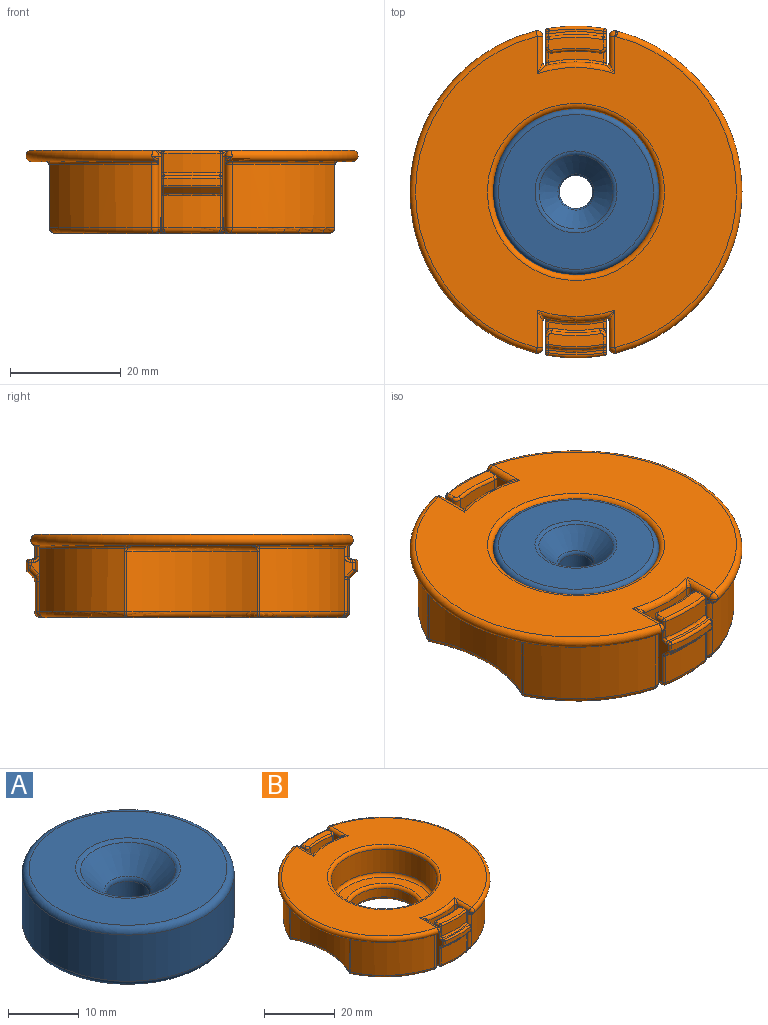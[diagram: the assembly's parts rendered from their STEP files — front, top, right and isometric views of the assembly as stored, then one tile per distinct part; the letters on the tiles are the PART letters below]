
ASSEMBLY  parts=2 mates=1
PART A: 10 faces, bbox 32.5x32.5x10 mm
  f0: cylinder r=3mm len=6mm, axis (0,0,-1), area 86.4mm2, adj f6,f7
  f1: cylinder r=15mm len=30mm, axis (0,0,-1), area 754mm2, adj f8,f9
  f2: plane 28x28mm, normal (0,0,1), area 443.1mm2, adj f5,f9
  f3: plane 28x28mm, normal (0,0,-1), area 565.5mm2, adj f7,f8
  f4: cone r=3mm half-angle=45deg, axis (0,0,1), area 151.7mm2, adj f5,f6
  f5: torus R=7.41mm, axis (0,0,1), area 34.7mm2, adj f2,f4
  f6: torus R=4mm, axis (0,0,-1), area 15.3mm2, adj f0,f4
  f7: torus R=4mm, axis (0,0,1), area 33.2mm2, adj f0,f3
  f8: torus R=14mm, axis (0,0,1), area 144.5mm2, adj f1,f3
  f9: torus R=14mm, axis (0,0,1), area 144.5mm2, adj f1,f2
PART B: 237 faces, bbox 65.5x81.4x21.4 mm
  f0: plane 25.09x5.42mm, normal (0,0,-1), area 77.3mm2, adj f1,f234,f235,f236
  f1: bspline ~2.39x0.69mm, area 0.5mm2, adj f0,f2,f233
  f2: torus R=29mm, axis (0,0,1), area 19.7mm2, adj f1,f3,f232,f236
  f3: torus R=1.5mm, axis (0,0,1), area 1.1mm2, adj f2,f4,f230,f231
  f4: bspline ~1.67x1mm, area 0.4mm2, adj f3,f5,f229
  f5: cylinder r=0.5mm len=0.5mm, axis (0,1,0), area 0.1mm2, adj f4,f6,f229,f230
  f6: torus R=0.5mm, axis (0,0,1), area 0.2mm2, adj f5,f7,f228,f230
  f7: cylinder r=1mm len=1.24mm, axis (0,0,1), area 0.5mm2, adj f6,f8,f228,f229
  f8: sphere r=1mm, area 2.3mm2, adj f7,f9,f236
  f9: cylinder r=1mm len=6.76mm, axis (0,-1,0), area 9.1mm2, adj f8,f10,f227,f229
  f10: plane 58x56.29mm, normal (0,0,1), area 1653.5mm2, adj f9,f11,f221,f222,f223,f224,f225,f226
  f11: torus R=22.5mm, axis (0,0,1), area 19.9mm2, adj f10,f12,f220,f227
  f12: bspline ~1.98x1.62mm, area 0.7mm2, adj f11,f13,f225
  f13: cylinder r=0.5mm len=13mm, axis (0,0,1), area 11.2mm2, adj f12,f14,f217,f218,f219,f220
  f14: bspline ~1.2x1.19mm, area 0.6mm2, adj f13,f15,f216,f217,f220
  f15: torus R=24mm, axis (0,0,1), area 7.8mm2, adj f14,f16,f215,f220
  f16: bspline ~1.22x1.13mm, area 0.6mm2, adj f15,f17,f213,f214,f220
  f17: cylinder r=0.5mm len=1.5mm, axis (0,0,1), area 0.6mm2, adj f16,f18,f212,f214
  f18: bspline ~1.38x1.19mm, area 0.4mm2, adj f17,f19,f210,f211
  f19: bspline ~1.98x1.62mm, area 0.7mm2, adj f18,f20,f210,f214
  f20: cylinder r=1mm len=5.21mm, axis (0,1,0), area 6.6mm2, adj f19,f21,f156,f229
  f21: sphere r=1mm, area 1.2mm2, adj f20,f22,f231
  f22: torus R=27.5mm, axis (0,0,1), area 38.3mm2, adj f21,f23,f156,f232
  f23: bspline ~1.14x1.11mm, area 0.3mm2, adj f22,f24,f155
  f24: torus R=27.68mm, axis (0,0,1), area 38.5mm2, adj f23,f25,f154,f156
  f25: bspline ~1.14x1.11mm, area 0.3mm2, adj f24,f26,f153
  f26: torus R=27.5mm, axis (0,0,1), area 38.3mm2, adj f25,f27,f151,f156
  f27: sphere r=1mm, area 1.8mm2, adj f26,f28,f150
  f28: cylinder r=1mm len=5.21mm, axis (0,1,0), area 6.6mm2, adj f27,f29,f140,f156
  f29: bspline ~1.98x1.62mm, area 0.7mm2, adj f28,f30,f137,f138
  f30: bspline ~1.38x1.19mm, area 0.4mm2, adj f29,f31,f136,f137
  f31: cylinder r=0.5mm len=1.5mm, axis (0,0,1), area 0.6mm2, adj f30,f32,f135,f138
  f32: bspline ~1.2x1.19mm, area 0.6mm2, adj f31,f33,f133,f134,f138
  f33: cylinder r=23.5mm len=10.77mm, axis (0,0,1), area 114.2mm2, adj f32,f34,f131,f133,f138,f222
  f34: bspline ~1.22x1.13mm, area 0.6mm2, adj f33,f35,f130,f131,f133
  f35: cylinder r=0.5mm len=1.5mm, axis (0,0,1), area 0.6mm2, adj f34,f36,f129,f131
  f36: bspline ~1.38x1.19mm, area 0.4mm2, adj f35,f37,f38,f87
  f37: torus R=22.5mm, axis (0,0,1), area 1.3mm2, adj f36,f87,f156
  f38: cylinder r=1mm len=5.5mm, axis (0,1,0), area 7.4mm2, adj f36,f39,f129,f156
  f39: bspline ~1.13x1mm, area 0.5mm2, adj f38,f40,f86
  f40: cylinder r=0.5mm len=5.79mm, axis (0,0,1), area 4mm2, adj f39,f41,f85,f129
  f41: bspline ~0.99x0.68mm, area 0.4mm2, adj f40,f42,f84,f129
  f42: bspline ~16.41x16.19mm, area 1.2mm2, adj f41,f43,f83,f129
  f43: cone r=30mm half-angle=45deg, axis (0,0,1), area 17.4mm2, adj f42,f44,f79,f84
  f44: torus R=29.5mm, axis (0,0,-1), area 4mm2, adj f43,f45,f78,f83
  f45: cylinder r=30mm len=10.17mm, axis (0,0,1), area 13.2mm2, adj f44,f46,f76,f77
  f46: torus R=29.5mm, axis (0,0,1), area 8mm2, adj f45,f47,f74,f75
  f47: plane 10x0.93mm, normal (0,0,1), area 5mm2, adj f46,f48,f72,f73
  f48: torus R=29mm, axis (0,0,1), area 7.9mm2, adj f47,f49,f70,f71
  f49: bspline ~1.25x1.18mm, area 0.8mm2, adj f48,f50,f73,f129
  f50: cylinder r=0.5mm len=3.5mm, axis (0,0,1), area 2.4mm2, adj f49,f51,f71,f129
  f51: sphere r=0.5mm, area 0.3mm2, adj f50,f52,f69
  f52: torus R=28mm, axis (0,0,1), area 8mm2, adj f51,f53,f67,f71
  f53: plane 10x2.39mm, normal (0,0,1), area 20mm2, adj f52,f54,f64,f65,f66,f69
  f54: torus R=0.5mm, axis (0,0,1), area 1.1mm2, adj f53,f55,f64,f69
  f55: cylinder r=1mm len=11mm, axis (0,0,1), area 19.2mm2, adj f54,f56,f63,f129
  f56: torus R=1.5mm, axis (0,0,1), area 1mm2, adj f55,f57,f61,f62
  f57: torus R=25mm, axis (0,0,1), area 6.8mm2, adj f56,f58,f61,f63
  f58: torus R=1.5mm, axis (0,0,1), area 1mm2, adj f57,f59,f60,f61
  f59: cylinder r=1mm len=11mm, axis (0,0,1), area 19.2mm2, adj f58,f63,f65,f135
  f60: bspline ~1.67x1mm, area 0.4mm2, adj f58,f134,f135
  f61: plane 10x1.53mm, normal (0,0,1), area 10.2mm2, adj f56,f57,f58,f130,f133,f134
  f62: bspline ~1.67x1mm, area 0.5mm2, adj f56,f129,f130
  f63: cylinder r=25.5mm len=11mm, axis (0,0,1), area 95.7mm2, adj f55,f57,f59,f64
  f64: torus R=26mm, axis (0,0,1), area 6.9mm2, adj f53,f54,f63,f65
  f65: torus R=0.5mm, axis (0,0,1), area 1.1mm2, adj f53,f59,f64,f66
  f66: cylinder r=0.5mm len=1.44mm, axis (0,1,0), area 1.1mm2, adj f53,f65,f67,f135
  f67: sphere r=0.5mm, area 0.3mm2, adj f52,f66,f68
  f68: cylinder r=0.5mm len=3.5mm, axis (0,0,1), area 2.4mm2, adj f67,f70,f71,f135
  f69: cylinder r=0.5mm len=1.44mm, axis (0,-1,0), area 1.1mm2, adj f51,f53,f54,f129
  f70: bspline ~1.22x1.18mm, area 0.8mm2, adj f48,f68,f72,f135
  f71: cylinder r=28.5mm len=10.18mm, axis (0,0,1), area 35.8mm2, adj f48,f50,f52,f68
  f72: cylinder r=0.5mm len=0.51mm, axis (0,1,0), area 0.4mm2, adj f47,f70,f74,f135
  f73: cylinder r=0.5mm len=0.51mm, axis (0,-1,0), area 0.4mm2, adj f47,f49,f75,f129
  f74: sphere r=0.5mm, area 0.4mm2, adj f46,f72,f76
  f75: sphere r=0.5mm, area 0.2mm2, adj f46,f73,f77
  f76: cylinder r=0.5mm len=1.29mm, axis (0,0,1), area 0.9mm2, adj f45,f74,f78,f135
  f77: cylinder r=0.5mm len=1.29mm, axis (0,0,1), area 0.9mm2, adj f45,f75,f83,f129
  f78: sphere r=0.5mm, area 0.1mm2, adj f44,f76,f79
  f79: bspline ~16.41x16.19mm, area 1.2mm2, adj f43,f78,f80,f135
  f80: bspline ~0.96x0.74mm, area 0.4mm2, adj f79,f81,f84,f135
  f81: cylinder r=0.5mm len=5.79mm, axis (0,0,1), area 4mm2, adj f80,f82,f85,f135
  f82: bspline ~1.13x1mm, area 0.5mm2, adj f81,f86,f136
  f83: sphere r=0.5mm, area 0.1mm2, adj f42,f44,f77
  f84: torus R=29mm, axis (0,0,-1), area 4mm2, adj f41,f43,f80,f85
  f85: cylinder r=28.5mm len=10.18mm, axis (0,0,1), area 59.3mm2, adj f40,f81,f84,f86
  f86: torus R=27.5mm, axis (0,0,1), area 15.2mm2, adj f39,f82,f85,f156
  f87: bspline ~1.98x1.62mm, area 0.7mm2, adj f36,f37,f88,f131
  f88: cylinder r=1mm len=5.21mm, axis (0,-1,0), area 6.6mm2, adj f87,f89,f128,f156
  f89: sphere r=1mm, area 1.8mm2, adj f88,f90,f127
  f90: torus R=27.5mm, axis (0,0,1), area 38.3mm2, adj f89,f91,f126,f156
  f91: bspline ~1.14x1.11mm, area 0.3mm2, adj f90,f92,f125
  f92: cylinder r=0.5mm len=11mm, axis (0,0,-1), area 5mm2, adj f91,f93,f124,f126
  f93: cylinder r=26.68mm len=23.57mm, axis (0,0,1), area 268.6mm2, adj f92,f94,f123,f125
  f94: torus R=25.68mm, axis (0,0,1), area 35.7mm2, adj f93,f95,f122,f124
  f95: plane 25.09x5.42mm, normal (0,0,-1), area 77.3mm2, adj f94,f96,f106,f224
  f96: bspline ~2.18x0.58mm, area 0.5mm2, adj f95,f97,f124
  f97: torus R=29mm, axis (0,0,1), area 19.7mm2, adj f96,f98,f126,f224
  f98: torus R=1.5mm, axis (0,0,1), area 1.1mm2, adj f97,f99,f105,f127
  f99: bspline ~1.67x1mm, area 0.4mm2, adj f98,f100,f128
  f100: cylinder r=0.5mm len=0.5mm, axis (0,1,0), area 0.1mm2, adj f99,f101,f105,f128
  f101: torus R=0.5mm, axis (0,0,1), area 0.2mm2, adj f100,f102,f104,f105
  f102: cylinder r=1mm len=1.24mm, axis (0,0,1), area 0.5mm2, adj f101,f103,f104,f128
  f103: sphere r=1mm, area 1.8mm2, adj f102,f223,f224
  f104: bspline ~1.25x1.06mm, area 0.6mm2, adj f101,f102,f224
  f105: plane 0.88x0.25mm, normal (0,0,-1), area 0.1mm2, adj f98,f100,f101,f224
  f106: bspline ~2.39x0.69mm, area 0.5mm2, adj f95,f107,f122
  f107: torus R=29mm, axis (0,0,1), area 19.7mm2, adj f106,f108,f121,f224
  f108: torus R=1.5mm, axis (0,0,1), area 1.1mm2, adj f107,f109,f115,f120
  f109: bspline ~1.67x1mm, area 0.5mm2, adj f108,f110,f219
  f110: cylinder r=0.5mm len=0.5mm, axis (0,-1,0), area 0.1mm2, adj f109,f111,f120,f219
  f111: torus R=0.5mm, axis (0,0,1), area 0.2mm2, adj f110,f112,f114,f120
  f112: cylinder r=1mm len=1.24mm, axis (0,0,1), area 0.5mm2, adj f111,f113,f114,f219
  f113: sphere r=1mm, area 1.2mm2, adj f112,f224,f225
  f114: bspline ~1.25x1.06mm, area 0.6mm2, adj f111,f112,f224
  f115: cylinder r=1mm len=11.5mm, axis (0,0,1), area 21mm2, adj f108,f116,f121,f219
  f116: sphere r=1mm, area 1.2mm2, adj f115,f117,f118
  f117: cylinder r=1mm len=5.21mm, axis (0,-1,0), area 6.6mm2, adj f116,f156,f218,f219
  f118: torus R=27.5mm, axis (0,0,1), area 38.3mm2, adj f116,f119,f121,f156
  f119: bspline ~1.14x1.11mm, area 0.3mm2, adj f118,f123,f125
  f120: plane 0.88x0.25mm, normal (0,0,-1), area 0.1mm2, adj f108,f110,f111,f224
  f121: cylinder r=28.5mm len=18.54mm, axis (0,0,1), area 285.3mm2, adj f107,f115,f118,f122,f123
  f122: bspline ~2.27x1.71mm, area 0.4mm2, adj f94,f106,f121,f123
  f123: cylinder r=0.5mm len=11mm, axis (0,0,-1), area 5mm2, adj f93,f119,f121,f122
  f124: bspline ~2.27x1.71mm, area 0.4mm2, adj f92,f94,f96,f126
  f125: torus R=27.68mm, axis (0,0,1), area 38.5mm2, adj f91,f93,f119,f156
  f126: cylinder r=28.5mm len=18.54mm, axis (0,0,1), area 285.3mm2, adj f90,f92,f97,f124,f127
  f127: cylinder r=1mm len=11.5mm, axis (0,0,1), area 21mm2, adj f89,f98,f126,f128
  f128: plane 13.54x5.32mm, normal (1,0,0), area 43.3mm2, adj f88,f99,f100,f102,f127,f131,f223
  f129: plane 13.5x5.84mm, normal (-1,0,0), area 27.5mm2, adj f35,f38,f40,f41,f42,f49,f50,f55
  f130: cylinder r=0.5mm len=1.46mm, axis (0,-1,0), area 1.1mm2, adj f34,f61,f62,f129
  f131: cylinder r=0.5mm len=13mm, axis (0,0,1), area 11.2mm2, adj f33,f34,f35,f87,f128,f132
  f132: bspline ~1.98x1.62mm, area 0.7mm2, adj f131,f222,f223
  f133: torus R=24mm, axis (0,0,1), area 7.8mm2, adj f32,f33,f34,f61
  f134: cylinder r=0.5mm len=1.46mm, axis (0,1,0), area 1.1mm2, adj f32,f60,f61,f135
  f135: plane 14.04x6.38mm, normal (1,0,0), area 27.5mm2, adj f31,f59,f60,f66,f68,f70,f72,f76
  f136: cylinder r=1mm len=5.5mm, axis (0,-1,0), area 7.4mm2, adj f30,f82,f135,f156
  f137: torus R=22.5mm, axis (0,0,1), area 1.3mm2, adj f29,f30,f156
  f138: cylinder r=0.5mm len=13mm, axis (0,0,1), area 11.2mm2, adj f29,f31,f32,f33,f139,f140
  f139: bspline ~1.98x1.62mm, area 0.7mm2, adj f138,f221,f222
  f140: plane 13x4.78mm, normal (-1,0,0), area 43.3mm2, adj f28,f138,f141,f148,f149,f150,f221
  f141: cylinder r=1mm len=1.24mm, axis (0,0,1), area 0.5mm2, adj f140,f142,f143,f144
  f142: sphere r=1mm, area 1.8mm2, adj f141,f221,f236
  f143: bspline ~1.23x1mm, area 0.6mm2, adj f141,f144,f236
  f144: torus R=0.5mm, axis (0,0,1), area 0.2mm2, adj f141,f143,f145,f148
  f145: plane 0.88x0.25mm, normal (0,0,-1), area 0.1mm2, adj f144,f146,f148,f236
  f146: torus R=1.5mm, axis (0,0,1), area 1.1mm2, adj f145,f147,f149,f150
  f147: torus R=29mm, axis (0,0,1), area 19.7mm2, adj f146,f151,f235,f236
  f148: cylinder r=0.5mm len=0.5mm, axis (0,-1,0), area 0.1mm2, adj f140,f144,f145,f149
  f149: bspline ~1.67x1mm, area 0.5mm2, adj f140,f146,f148
  f150: cylinder r=1mm len=11.5mm, axis (0,0,1), area 21mm2, adj f27,f140,f146,f151
  f151: cylinder r=28.5mm len=18.54mm, axis (0,0,1), area 285.3mm2, adj f26,f147,f150,f152,f153
  f152: bspline ~2.27x1.71mm, area 0.4mm2, adj f151,f153,f234,f235
  f153: cylinder r=0.5mm len=11mm, axis (0,0,-1), area 5mm2, adj f25,f151,f152,f154
  f154: cylinder r=26.68mm len=23.57mm, axis (0,0,1), area 268.6mm2, adj f24,f153,f155,f234
  f155: cylinder r=0.5mm len=11mm, axis (0,0,-1), area 5mm2, adj f23,f154,f232,f233
  f156: plane 55x49.48mm, normal (0,0,-1), area 1766.3mm2, adj f20,f22,f24,f26,f28,f37,f38,f86
  f157: torus R=27.5mm, axis (0,0,1), area 14.5mm2, adj f156,f158,f198,f199,f200
  f158: sphere r=1mm, area 0.5mm2, adj f157,f159,f211
  f159: cylinder r=1mm len=5.59mm, axis (0,0,1), area 7.9mm2, adj f158,f160,f198,f212
  f160: bspline ~1.99x1.37mm, area 1.6mm2, adj f159,f161,f197,f212
  f161: bspline ~20.43x20.21mm, area 2.5mm2, adj f160,f162,f196,f212
  f162: bspline ~1.32x1.14mm, area 0.6mm2, adj f161,f163,f194,f195
  f163: cylinder r=30mm len=10.17mm, axis (0,0,1), area 12.9mm2, adj f162,f164,f192,f193,f194,f195
  f164: torus R=29.5mm, axis (0,0,1), area 8mm2, adj f163,f165,f190,f191
  f165: sphere r=0.5mm, area 0.2mm2, adj f164,f166,f195
  f166: cylinder r=0.5mm len=0.51mm, axis (0,1,0), area 0.4mm2, adj f165,f167,f190,f212
  f167: bspline ~1.25x1.18mm, area 0.8mm2, adj f166,f168,f189,f212
  f168: torus R=29mm, axis (0,0,1), area 7.9mm2, adj f167,f169,f188,f190
  f169: bspline ~1.22x1.18mm, area 0.8mm2, adj f168,f170,f171,f184
  f170: cylinder r=0.5mm len=0.51mm, axis (0,-1,0), area 0.4mm2, adj f169,f184,f190,f191
  f171: cylinder r=0.5mm len=3.5mm, axis (0,0,1), area 2.4mm2, adj f169,f172,f184,f188
  f172: sphere r=0.5mm, area 0.4mm2, adj f171,f173,f183
  f173: cylinder r=0.5mm len=1.44mm, axis (0,-1,0), area 1.1mm2, adj f172,f174,f182,f184
  f174: plane 10x2.39mm, normal (0,0,1), area 20mm2, adj f173,f175,f177,f181,f182,f183
  f175: cylinder r=0.5mm len=1.44mm, axis (0,1,0), area 1.1mm2, adj f174,f176,f177,f212
  f176: sphere r=0.5mm, area 0.5mm2, adj f175,f183,f189
  f177: torus R=0.5mm, axis (0,0,1), area 1.1mm2, adj f174,f175,f178,f181
  f178: cylinder r=1mm len=12mm, axis (0,0,1), area 20.3mm2, adj f177,f179,f212,f213,f215
  f179: cylinder r=25.5mm len=11.5mm, axis (0,0,1), area 100.1mm2, adj f178,f180,f181,f215
  f180: cylinder r=1mm len=12mm, axis (0,0,1), area 20.3mm2, adj f179,f182,f184,f215,f216
  f181: torus R=26mm, axis (0,0,1), area 6.9mm2, adj f174,f177,f179,f182
  f182: torus R=0.5mm, axis (0,0,1), area 1.1mm2, adj f173,f174,f180,f181
  f183: torus R=28mm, axis (0,0,1), area 8mm2, adj f172,f174,f176,f188
  f184: plane 13.5x5.84mm, normal (-1,0,0), area 23.4mm2, adj f169,f170,f171,f173,f180,f185,f186,f187
  f185: cylinder r=1mm len=5.59mm, axis (0,0,1), area 7.9mm2, adj f184,f186,f198,f199
  f186: bspline ~1.92x1.48mm, area 1.6mm2, adj f184,f185,f187,f197
  f187: bspline ~20.43x20.21mm, area 2.5mm2, adj f184,f186,f193,f196
  f188: cylinder r=28.5mm len=10.18mm, axis (0,0,1), area 35.8mm2, adj f168,f171,f183,f189
  f189: cylinder r=0.5mm len=3.5mm, axis (0,0,1), area 2.4mm2, adj f167,f176,f188,f212
  f190: plane 10x0.93mm, normal (0,0,1), area 5mm2, adj f164,f166,f168,f170
  f191: sphere r=0.5mm, area 0.5mm2, adj f164,f170,f192
  f192: cylinder r=0.5mm len=0.67mm, axis (0,0,1), area 0.5mm2, adj f163,f184,f191,f193
  f193: bspline ~1.32x1.14mm, area 0.6mm2, adj f163,f187,f192,f194
  f194: torus R=29.5mm, axis (0,0,-1), area 3.6mm2, adj f162,f163,f193,f196
  f195: cylinder r=0.5mm len=0.67mm, axis (0,0,1), area 0.5mm2, adj f162,f163,f165,f212
  f196: cone r=30mm half-angle=45deg, axis (0,0,1), area 13.9mm2, adj f161,f187,f194,f197
  f197: torus R=29.5mm, axis (0,0,-1), area 7.3mm2, adj f160,f186,f196,f198
  f198: cylinder r=28.5mm len=9.33mm, axis (0,0,1), area 52.3mm2, adj f157,f159,f185,f197
  f199: sphere r=1mm, area 0.9mm2, adj f157,f185,f201
  f200: sphere r=1mm, area 0.2mm2, adj f157,f211
  f201: cylinder r=1mm len=5.08mm, axis (0,1,0), area 7mm2, adj f156,f184,f199,f202
  f202: bspline ~1.38x1.19mm, area 0.4mm2, adj f201,f203,f217,f218
  f203: torus R=22.5mm, axis (0,0,1), area 1.3mm2, adj f156,f202,f218
  f204: torus R=11mm, axis (0,0,1), area 102.3mm2, adj f156,f205
  f205: cylinder r=10mm len=20mm, axis (0,0,1), area 188.5mm2, adj f204,f206
  f206: torus R=11mm, axis (0,0,1), area 102.3mm2, adj f205,f207
  f207: plane 28x28mm, normal (0,0,1), area 235.6mm2, adj f206,f208
  f208: torus R=14mm, axis (0,0,1), area 144.5mm2, adj f207,f209
  f209: cylinder r=15mm len=30mm, axis (0,0,1), area 754mm2, adj f208,f226
  f210: torus R=22.5mm, axis (0,0,1), area 1.3mm2, adj f18,f19,f156
  f211: cylinder r=1mm len=5.08mm, axis (0,-1,0), area 7mm2, adj f18,f156,f158,f200,f212
  f212: plane 13.5x5.84mm, normal (1,0,0), area 23.4mm2, adj f17,f159,f160,f161,f166,f167,f175,f178
  f213: cylinder r=0.5mm len=2.88mm, axis (0,1,0), area 1.8mm2, adj f16,f178,f212,f215
  f214: cylinder r=0.5mm len=13mm, axis (0,0,1), area 11.2mm2, adj f16,f17,f19,f220,f227,f229
  f215: plane 10x2.03mm, normal (0,0,1), area 15.2mm2, adj f15,f178,f179,f180,f213,f216
  f216: cylinder r=0.5mm len=2.88mm, axis (0,-1,0), area 1.8mm2, adj f14,f180,f184,f215
  f217: cylinder r=0.5mm len=1.5mm, axis (0,0,1), area 0.6mm2, adj f13,f14,f184,f202
  f218: bspline ~1.98x1.62mm, area 0.7mm2, adj f13,f117,f202,f203
  f219: plane 13x4.78mm, normal (1,0,0), area 43.3mm2, adj f13,f109,f110,f112,f115,f117,f225
  f220: cylinder r=23.5mm len=10.77mm, axis (0,0,1), area 114.2mm2, adj f11,f13,f14,f15,f16,f214
  f221: cylinder r=1mm len=6.76mm, axis (0,-1,0), area 9.1mm2, adj f10,f139,f140,f142
  f222: torus R=22.5mm, axis (0,0,1), area 19.9mm2, adj f10,f33,f132,f139
  f223: cylinder r=1mm len=6.76mm, axis (0,1,0), area 9.1mm2, adj f10,f103,f128,f132
  f224: torus R=29mm, axis (0,0,1), area 247.9mm2, adj f10,f95,f97,f103,f104,f105,f107,f113
  f225: cylinder r=1mm len=6.76mm, axis (0,1,0), area 9.1mm2, adj f10,f12,f113,f219
  f226: torus R=16mm, axis (0,0,1), area 151.6mm2, adj f10,f209
  f227: bspline ~1.98x1.62mm, area 0.7mm2, adj f9,f11,f214
  f228: bspline ~1.25x1.06mm, area 0.6mm2, adj f6,f7,f236
  f229: plane 13.54x5.32mm, normal (-1,0,0), area 43.3mm2, adj f4,f5,f7,f9,f20,f214,f231
  f230: plane 0.88x0.25mm, normal (0,0,-1), area 0.1mm2, adj f3,f5,f6,f236
  f231: cylinder r=1mm len=11.5mm, axis (0,0,1), area 21mm2, adj f3,f21,f229,f232
  f232: cylinder r=28.5mm len=18.54mm, axis (0,0,1), area 285.3mm2, adj f2,f22,f155,f231,f233
  f233: bspline ~2.27x1.71mm, area 0.4mm2, adj f1,f155,f232,f234
  f234: torus R=25.68mm, axis (0,0,1), area 35.7mm2, adj f0,f152,f154,f233
  f235: bspline ~2.18x0.58mm, area 0.5mm2, adj f0,f147,f152
  f236: torus R=29mm, axis (0,0,1), area 247.9mm2, adj f0,f2,f8,f10,f142,f143,f145,f147
PLACE A t=(0,0,-10)mm
PLACE B at identity
MATE fastened A.f0 <-> B.f107  axis (0,0,1) through (0,0,0)mm
